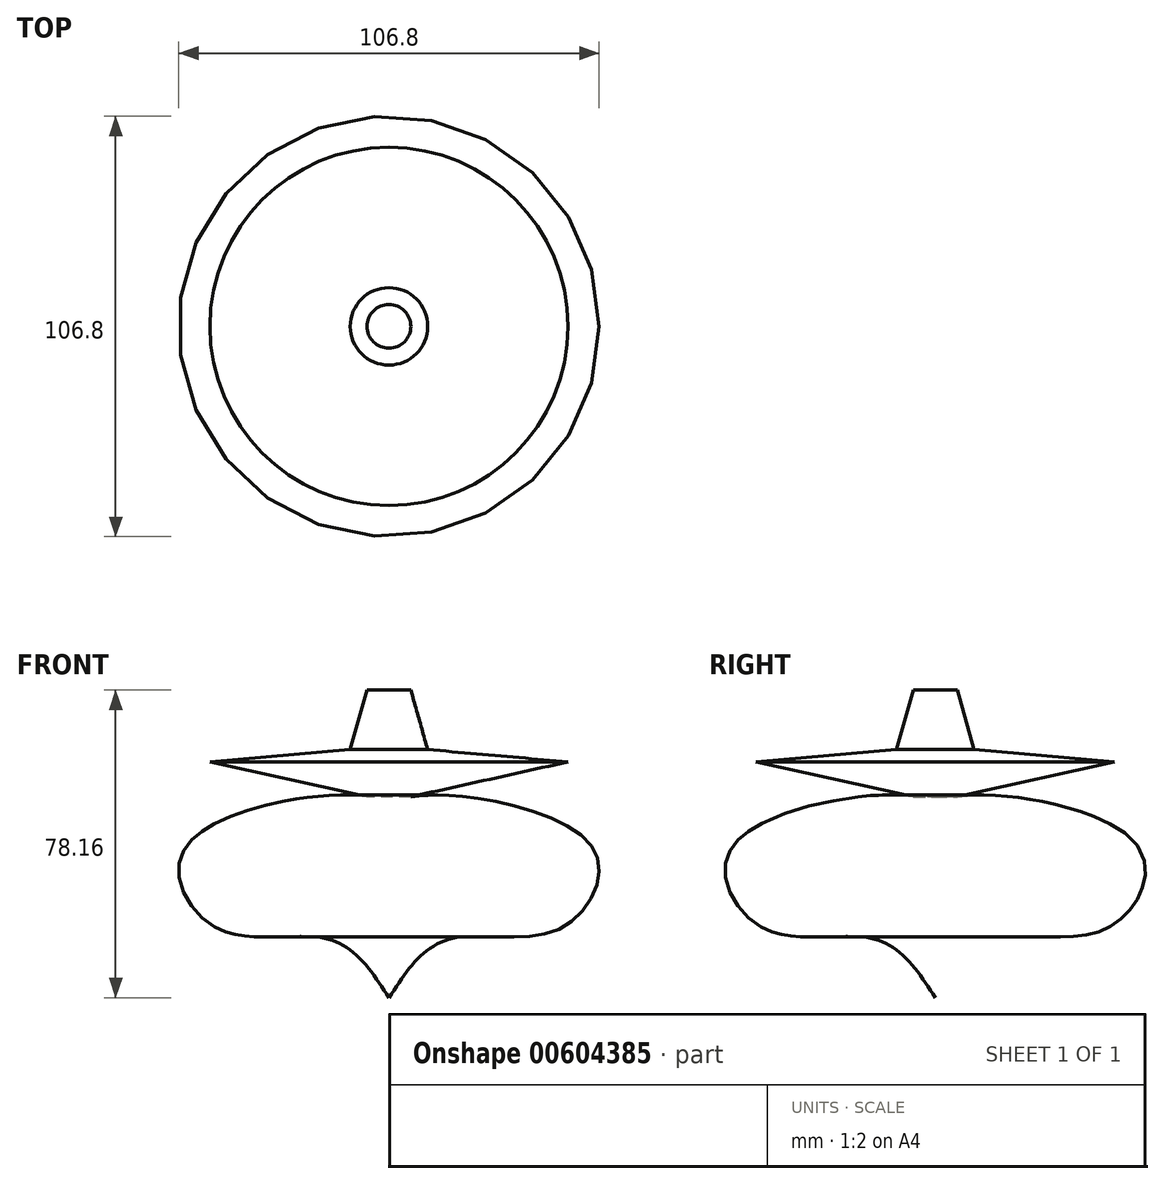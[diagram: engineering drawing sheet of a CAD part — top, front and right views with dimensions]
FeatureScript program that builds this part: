
annotation { "Feature Type Name" : "Feature", "Feature Type Description" : "" }
export const myFeature = defineFeature(function(context is Context, id is Id, definition is map)
    precondition{}
    {
        {
            var Q0;
            Q0=qCreatedBy(makeId("Front.planeOp"),FACE);
            var sketch = newSketch(context, id + "F0", { "sketchPlane" : qUnion([Q0])});
            skFitSpline(sketch, "E0", {"points": [v(0, 0) * mm, v(15.26, 14.83) * mm, v(43.21, 17.4) * mm, v(52.34, 37.08) * mm, v(19.25, 51.06) * mm, v(5.56, 51.06) * mm], "startDerivative": vector(65.85, 101.6) * mm, "endDerivative": vector(-70.6, -7.3) * mm});
            skLineSegment(sketch, "E1", {"start": v(5.56, 51.06) * mm, "end": v(45.5, 59.9) * mm});
            skLineSegment(sketch, "E2", {"start": v(45.5, 59.9) * mm, "end": v(9.84, 63.04) * mm});
            skLineSegment(sketch, "E3", {"start": v(9.84, 63.04) * mm, "end": v(5.56, 78.16) * mm});
            skLineSegment(sketch, "E4", {"start": v(5.56, 78.16) * mm, "end": v(0, 78.16) * mm});
            skLineSegment(sketch, "E5", {"start": v(0, 78.16) * mm, "end": v(0, 0) * mm});
            skSolve(sketch);
        }
        {
            var Q0;
            Q0 = qSketchRegion(id + "F0", true);
            var Q1;
            Q1=sQuery(id+"F0.wireOp",EDGE,"E5");
            revolve(context, id + "F1", {"entities" : qUnion([Q0]), "axis" : qUnion([Q1]), "revolveType" : RevolveType.FULL});
        }
    });
